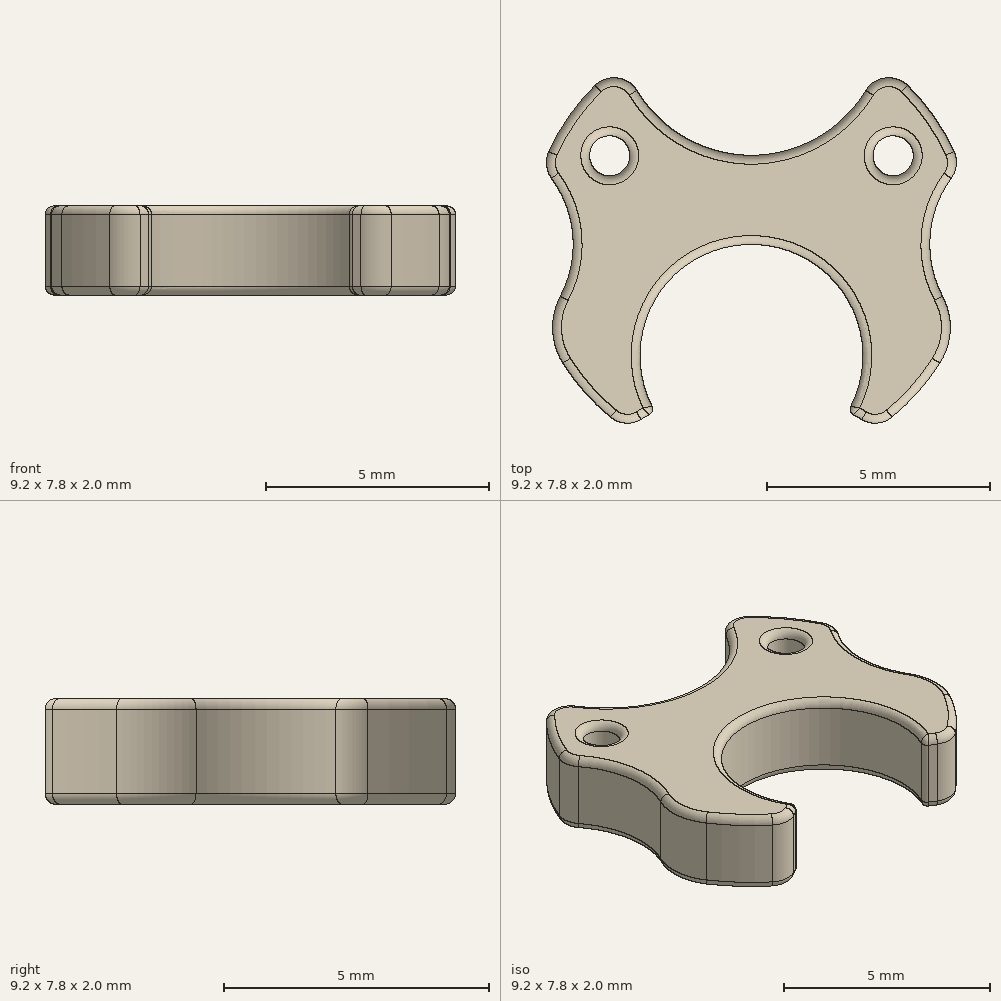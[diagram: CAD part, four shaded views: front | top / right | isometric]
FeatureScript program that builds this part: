
annotation { "Feature Type Name" : "Feature", "Feature Type Description" : "" }
export const myFeature = defineFeature(function(context is Context, id is Id, definition is map)
    precondition{}
    {
        {
            var Q0;
            Q0=qCreatedBy(makeId("Top.planeOp"),FACE);
            var sketch = newSketch(context, id + "F0", { "sketchPlane" : qUnion([Q0])});
            skArc(sketch, "E0", {"start": v(2.17, -1.25) * mm, "mid": v(0, 2.5) * mm, "end": v(-2.17, -1.25) * mm});
            skArc(sketch, "E1", {"start": v(2.82, -1.63) * mm, "mid": v(3.94, -0.57) * mm, "end": v(4.7, 0.77) * mm});
            skLineSegment(sketch, "E2", {"start": v(2.17, -1.25) * mm, "end": v(2.82, -1.63) * mm});
            skLineSegment(sketch, "E3", {"start": v(-2.17, -1.25) * mm, "end": v(-2.82, -1.63) * mm});
            skArc(sketch, "E4", {"start": v(-2.86, 6.6) * mm, "mid": v(0, 4.5) * mm, "end": v(2.86, 6.6) * mm});
            skArc(sketch, "E5", {"start": v(4.7, 4.23) * mm, "mid": v(4, 2.5) * mm, "end": v(4.7, 0.77) * mm});
            skArc(sketch, "E6", {"start": v(-4.7, 0.77) * mm, "mid": v(-4, 2.5) * mm, "end": v(-4.7, 4.23) * mm});
            skArc(sketch, "E7.trimOffspring", {"start": v(4.7, 4.23) * mm, "mid": v(3.96, 5.55) * mm, "end": v(2.86, 6.6) * mm});
            skArc(sketch, "E8.trimOffspring", {"start": v(-2.86, 6.6) * mm, "mid": v(-3.96, 5.55) * mm, "end": v(-4.7, 4.23) * mm});
            skArc(sketch, "E9.trimOffspring", {"start": v(-4.7, 0.77) * mm, "mid": v(-3.94, -0.57) * mm, "end": v(-2.82, -1.63) * mm});
            skPoint(sketch, "E10.orphan", {"position": v(-5.68, 2.5) * mm});
            skCircle(sketch, "E11", {"center": v(-3.18, 4.49) * mm, "radius": 0.45 * mm});
            skCircle(sketch, "E12.MirrorC", {"center": v(3.18, 4.49) * mm, "radius": 0.45 * mm});
            skPoint(sketch, "E13.start.orphan", {"position": v(6.75, 4.5) * mm});
            skPoint(sketch, "E14.end.orphan", {"position": v(0, 4.5) * mm});
            skSolve(sketch);
        }
        {
            var Q0;
            Q0 = qSketchRegion(id + "F0", true);
            extrude(context, id + "F1", {"entities" : qUnion([Q0]), "depth" : 2 * mm, "offsetDistance" : 25 * mm});
        }
        {
            var Q0;
            Q0=makeQuery(id+"F1.opExtrude","SWEPT_EDGE",EDGE,{"disambiguationData":[OSD([sQuery(id+"F0.wireOp",EDGE,"E3"),sQuery(id+"F0.wireOp",EDGE,"E9.trimOffspring")])]});
            var Q1;
            Q1=makeQuery(id+"F1.opExtrude","SWEPT_EDGE",EDGE,{"disambiguationData":[OSD([sQuery(id+"F0.wireOp",EDGE,"E1"),sQuery(id+"F0.wireOp",EDGE,"E2")])]});
            var Q2;
            Q2=makeQuery(id+"F1.opExtrude","SWEPT_EDGE",EDGE,{"disambiguationData":[OSD([sQuery(id+"F0.wireOp",EDGE,"E5"),sQuery(id+"F0.wireOp",EDGE,"E7.trimOffspring")])]});
            var Q3;
            Q3=makeQuery(id+"F1.opExtrude","SWEPT_EDGE",EDGE,{"disambiguationData":[OSD([sQuery(id+"F0.wireOp",EDGE,"E6"),sQuery(id+"F0.wireOp",EDGE,"E8.trimOffspring")])]});
            var Q4;
            Q4=makeQuery(id+"F1.opExtrude","SWEPT_EDGE",EDGE,{"disambiguationData":[OSD([sQuery(id+"F0.wireOp",EDGE,"E4"),sQuery(id+"F0.wireOp",EDGE,"E7.trimOffspring")])]});
            var Q5;
            Q5=makeQuery(id+"F1.opExtrude","SWEPT_EDGE",EDGE,{"disambiguationData":[OSD([sQuery(id+"F0.wireOp",EDGE,"E4"),sQuery(id+"F0.wireOp",EDGE,"E8.trimOffspring")])]});
            fillet(context, id + "F2", {"entities" : qUnion([Q0, Q1, Q2, Q3, Q4, Q5]), "radius" : 0.6 * mm, "tangentPropagation" : true, "allowEdgeOverflow" : false});
        }
        {
            var Q0;
            Q0=makeQuery(id+"F1.opExtrude","SWEPT_EDGE",EDGE,{"disambiguationData":[OSD([sQuery(id+"F0.wireOp",EDGE,"E1"),sQuery(id+"F0.wireOp",EDGE,"E5")])]});
            var Q1;
            Q1=makeQuery(id+"F1.opExtrude","SWEPT_EDGE",EDGE,{"disambiguationData":[OSD([sQuery(id+"F0.wireOp",EDGE,"E6"),sQuery(id+"F0.wireOp",EDGE,"E9.trimOffspring")])]});
            fillet(context, id + "F3", {"entities" : qUnion([Q0, Q1]), "radius" : 1.5 * mm, "tangentPropagation" : true, "allowEdgeOverflow" : false});
        }
        {
            var Q0;
            Q0=makeQuery(id+"F1.opExtrude","CAP_FACE",FACE,{"disambiguationData":[OSD([sQuery(id+"F0.wireOp",EDGE,"E0"),sQuery(id+"F0.wireOp",EDGE,"E1"),sQuery(id+"F0.wireOp",EDGE,"E2"),sQuery(id+"F0.wireOp",EDGE,"E3"),sQuery(id+"F0.wireOp",EDGE,"E4"),sQuery(id+"F0.wireOp",EDGE,"E5"),sQuery(id+"F0.wireOp",EDGE,"E6"),sQuery(id+"F0.wireOp",EDGE,"rKW5ost1-xDVr-MF5d-c13y-ktbk4sj4FXeu"),sQuery(id+"F0.wireOp",EDGE,"010c1898-611d-4e5f-818e-c9d4109e7d920.MirrorC"),sQuery(id+"F0.wireOp",EDGE,"E7.trimOffspring"),sQuery(id+"F0.wireOp",EDGE,"E8.trimOffspring"),sQuery(id+"F0.wireOp",EDGE,"E9.trimOffspring")])],"isStart":false});
            var Q1;
            Q1=makeQuery(id+"F1.opExtrude","CAP_FACE",FACE,{"disambiguationData":[OSD([sQuery(id+"F0.wireOp",EDGE,"E0"),sQuery(id+"F0.wireOp",EDGE,"E1"),sQuery(id+"F0.wireOp",EDGE,"E2"),sQuery(id+"F0.wireOp",EDGE,"E3"),sQuery(id+"F0.wireOp",EDGE,"E4"),sQuery(id+"F0.wireOp",EDGE,"E5"),sQuery(id+"F0.wireOp",EDGE,"E6"),sQuery(id+"F0.wireOp",EDGE,"rKW5ost1-xDVr-MF5d-c13y-ktbk4sj4FXeu"),sQuery(id+"F0.wireOp",EDGE,"010c1898-611d-4e5f-818e-c9d4109e7d920.MirrorC"),sQuery(id+"F0.wireOp",EDGE,"E7.trimOffspring"),sQuery(id+"F0.wireOp",EDGE,"E8.trimOffspring"),sQuery(id+"F0.wireOp",EDGE,"E9.trimOffspring")])],"isStart":true});
            fillet(context, id + "F4", {"entities" : qUnion([Q0, Q1]), "radius" : 0.2 * mm, "tangentPropagation" : true, "allowEdgeOverflow" : false});
        }
        {
            var Q0;
            Q0=makeQuery(id+"F1.opExtrude","SWEPT_EDGE",EDGE,{"disambiguationData":[OSD([sQuery(id+"F0.wireOp",EDGE,"E0"),sQuery(id+"F0.wireOp",EDGE,"E3")])]});
            var Q1;
            Q1=makeQuery(id+"F1.opExtrude","SWEPT_EDGE",EDGE,{"disambiguationData":[OSD([sQuery(id+"F0.wireOp",EDGE,"E0"),sQuery(id+"F0.wireOp",EDGE,"E2")])]});
            fillet(context, id + "F5", {"entities" : qUnion([Q0, Q1]), "radius" : 0.15 * mm, "tangentPropagation" : true, "allowEdgeOverflow" : false});
        }
    });
